# Revit family: CONV_Geberit_StorageUnits_IfoSense_SPMP60V1
name_source: partatom
category: Furniture
revit_build: Autodesk Revit 2016 (Build: 20150220_1215(x64)
units: mm (PartAtom-declared; Revit-internal decimal feet)

## family parameters
Always vertical = Yes
Cut with Voids When Loaded = No
OmniClass Number = 23.40.20.21
OmniClass Title = Toilet and Bath Specialties
Room Calculation Point = No
Shared = No
Work Plane-Based = No

## types (1)
- Ifo Sense furniture package SPMP 60 V1
    AssetType = Fixed
    BIMObjectName = CONV_Geberit_StorageUnits_IfoSense_SPMP60V1
    Brand = Ifo
    CabinetMainMaterial = White
    CabinetSecondaryMaterial = Porcelain, White
    Category = Sink Cabinet
    Collection = Ifo Sense
    Color = White
    ConvergoRefNr = 0132-1802-0016-SE
    Cost = 0 $
    DurationUnit = Year
    EANNumber = 7391515442861
    ExpiringDate = 12/2018
    Features = Water trap and adjustable suspension bracket
    IfcExportAs = IfcFurnitureType
    IfcExportType = CABINET
    MainColor = White
    Manufacturer = https://www.ifo.se
    ManufacturerName = Ifo (Geberit Group)
    ManufacturerURL = https://www.ifo.se
    Material = Wood, metal, porcelain
    Model = Ifo Sense furniture package SPMP 60 V1
    ModelNumber = 42640
    NBSDescription = Bathroom cabinets
    NBSReference = 45-35-72/318
    Name = StorageUnits_IfoSense_SPMP60V1
    NominalDepth = 514 mm  [stored 1.68635 ft]
    NominalHeight = 590 mm
    NominalLength = 622 mm
    ProductInformation = Ifo Sense complete furniture package with drawer, white, a soft closing box and a wash basin. A shelf, prepared for plumbing installation without extra hole picking. Straight grip in aluminum is included. Water trap and adjustable suspension bracket included. Mixer not included.
    ProductURL_DK = http://www.ifo.dk
    ProductURL_NO = http://www.ifosanitar.no
    ProductURL_SE = http://www.ifo.se
    Shape = Rectangular
    Size = 625x514x590 mm
    URL = https://www.ifo.se
    Uniclass2 = Pr_40_30_78_06
    Uniclass2015Description = Bathroom cabinets
    Uniclass2015Reference = Pr_40_30_78_03
    Version = 1
    VersionDate = 19/04/2018
    WarrantyDurationUnit = Year

note: [stored X ft] marks values corroborated as IEEE doubles in the binary element streams (Revit-internal decimal feet)

## geometry (parser evidence)
native form markers: Blend x8, Sweep x8
no freeform markers — native parametric forms only
